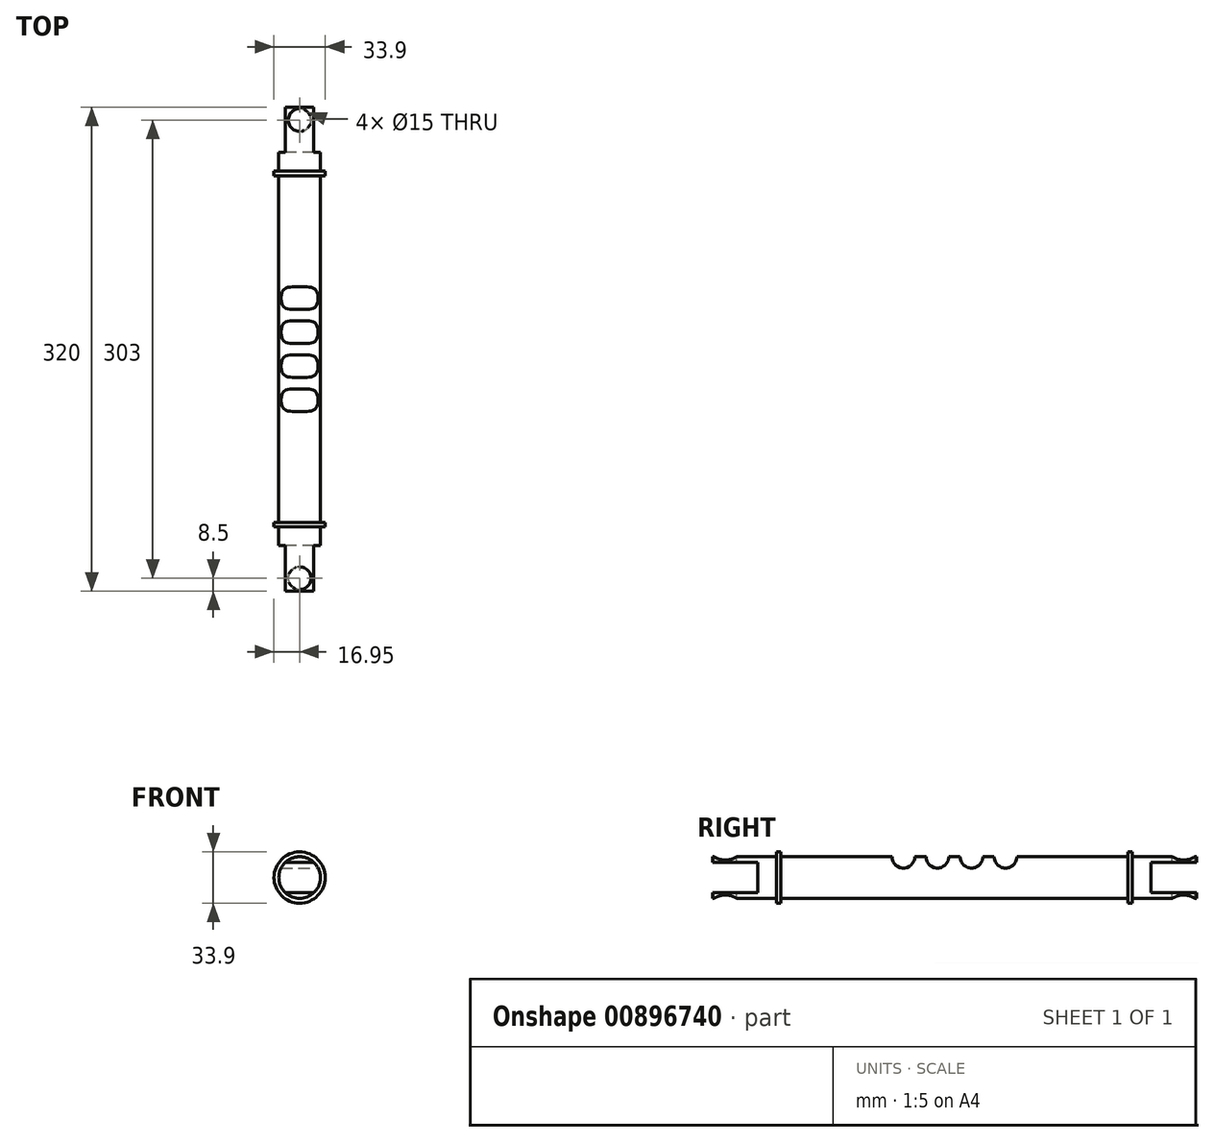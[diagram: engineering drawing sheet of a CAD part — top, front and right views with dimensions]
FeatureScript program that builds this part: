
annotation { "Feature Type Name" : "Feature", "Feature Type Description" : "" }
export const myFeature = defineFeature(function(context is Context, id is Id, definition is map)
    precondition{}
    {
        {
            var Q0;
            Q0=qCreatedBy(makeId("Front.planeOp"),FACE);
            var sketch = newSketch(context, id + "F0", { "sketchPlane" : qUnion([Q0])});
            skCircle(sketch, "E0", {"center": v(0, 0) * mm, "radius": 13.75 * mm});
            skSolve(sketch);
        }
        {
            var Q0;
            Q0=makeQuery(id+"F0.imprint","IMPRINT",FACE,{"disambiguationData":[TD([[makeQuery(id+"F0.imprint","IMPRINT",EDGE,{"derivedFrom":sQuery(id+"F0.wireOp",EDGE,"E0")}),1.0]])]});
            extrude(context, id + "F1", {"entities" : qUnion([Q0]), "depth" : 160 * mm, "offsetDistance" : 25 * mm});
        }
        {
            var Q0;
            Q0=qCreatedBy(makeId("Right.planeOp"),FACE);
            var sketch = newSketch(context, id + "F2", { "sketchPlane" : qUnion([Q0])});
            skLineSegment(sketch, "E1", {"start": v(-118.75, 13.75) * mm, "end": v(-133.75, 13.75) * mm});
            skArc(sketch, "E2", {"start": v(-156.25, 13.75) * mm, "mid": v(-148.75, 6.25) * mm, "end": v(-141.25, 13.75) * mm});
            skArc(sketch, "E3", {"start": v(-133.75, 13.75) * mm, "mid": v(-126.25, 6.25) * mm, "end": v(-118.75, 13.75) * mm});
            skPoint(sketch, "E4.orphan", {"position": v(-320, 13.75) * mm});
            skPoint(sketch, "E5.start.orphan", {"position": v(-160, 13.75) * mm});
            skPoint(sketch, "E6.orphan", {"position": v(0, 13.75) * mm});
            skPoint(sketch, "E7.orphan", {"position": v(0, -32.69) * mm});
            skLineSegment(sketch, "E8.trimOffspring", {"start": v(-141.25, 13.75) * mm, "end": v(-156.25, 13.75) * mm});
            skLineSegment(sketch, "E9", {"start": v(-160, 13.75) * mm, "end": v(-160, -55.7) * mm, "construction": true});
            skLineSegment(sketch, "E10", {"start": v(-9.6, 13.75) * mm, "end": v(-70.32, 13.75) * mm});
            skLineSegment(sketch, "E11.bottom", {"start": v(-42.38, 13.75) * mm, "end": v(-45.28, 13.75) * mm, "construction": true});
            skLineSegment(sketch, "E11.top", {"start": v(-42.38, 16.95) * mm, "end": v(-45.28, 16.95) * mm});
            skLineSegment(sketch, "E11.left", {"start": v(-42.38, 13.75) * mm, "end": v(-42.38, 16.95) * mm});
            skLineSegment(sketch, "E11.right", {"start": v(-45.28, 13.75) * mm, "end": v(-45.28, 16.95) * mm});
            skLineSegment(sketch, "E12", {"start": v(-1.56, 0) * mm, "end": v(-69.06, 0) * mm, "construction": true});
            skSolve(sketch);
        }
        {
            var Q0;
            Q0=makeQuery(id+"F2.imprint","IMPRINT",FACE,{"disambiguationData":[TD([[makeQuery(id+"F2.imprint","IMPRINT",EDGE,{"derivedFrom":sQuery(id+"F2.wireOp",EDGE,"nActoI5t-i0K3-M4oz-HlWf-qxMpZ23eEYZS")}),1.0]])]});
            var Q1;
            Q1=makeQuery(id+"F2.imprint","IMPRINT",FACE,{"disambiguationData":[TD([[makeQuery(id+"F2.imprint","IMPRINT",EDGE,{"derivedFrom":sQuery(id+"F2.wireOp",EDGE,"TeYV5sM8-H92p-1zPf-3jmj-FJZRoNFdDDTj")}),1.0]])]});
            var Q2;
            Q2=makeQuery(id+"F2.imprint","IMPRINT",FACE,{"disambiguationData":[TD([[makeQuery(id+"F2.imprint","IMPRINT",EDGE,{"derivedFrom":sQuery(id+"F2.wireOp",EDGE,"E2")}),1.0]])]});
            var Q3;
            Q3=makeQuery(id+"F2.imprint","IMPRINT",FACE,{"disambiguationData":[TD([[makeQuery(id+"F2.imprint","IMPRINT",EDGE,{"derivedFrom":sQuery(id+"F2.wireOp",EDGE,"E1")}),1.0]])]});
            extrude(context, id + "F3", {"entities" : qUnion([Q0, Q1, Q2, Q3]), "operationType" : NewBodyOperationType.REMOVE, "endBound" : BoundingType.SYMMETRIC, "oppositeDirection" : true, "depth" : 25 * mm, "offsetDistance" : 25 * mm});
        }
        {
            var Q0;
            Q0=qCreatedBy(makeId("Front.planeOp"),FACE);
            var sketch = newSketch(context, id + "F4", { "sketchPlane" : qUnion([Q0])});
            skLineSegment(sketch, "E13.bottom", {"start": v(18.75, 10) * mm, "end": v(-18.75, 10) * mm});
            skLineSegment(sketch, "E13.top", {"start": v(18.75, -10) * mm, "end": v(-18.75, -10) * mm});
            skLineSegment(sketch, "E13.left", {"start": v(18.75, 10) * mm, "end": v(18.75, -10) * mm});
            skLineSegment(sketch, "E13.right", {"start": v(-18.75, 10) * mm, "end": v(-18.75, -10) * mm});
            skPoint(sketch, "E13.middle", {"position": v(0, 0) * mm});
            skSolve(sketch);
        }
        {
            var Q0;
            Q0=makeQuery(id+"F4.imprint","IMPRINT",FACE,{"disambiguationData":[TD([[makeQuery(id+"F4.imprint","IMPRINT",EDGE,{"derivedFrom":sQuery(id+"F4.wireOp",EDGE,"E13.bottom")}),1.0]])]});
            extrude(context, id + "F5", {"entities" : qUnion([Q0]), "operationType" : NewBodyOperationType.REMOVE, "depth" : 30 * mm, "offsetDistance" : 25 * mm});
        }
        {
            var Q0;
            Q0=qCreatedBy(makeId("Top.planeOp"),FACE);
            var sketch = newSketch(context, id + "F6", { "sketchPlane" : qUnion([Q0])});
            skCircle(sketch, "E14", {"center": v(0, -8.5) * mm, "radius": 7.5 * mm});
            skSolve(sketch);
        }
        {
            var Q0;
            Q0=makeQuery(id+"F6.imprint","IMPRINT",FACE,{"disambiguationData":[TD([[makeQuery(id+"F6.imprint","IMPRINT",EDGE,{"derivedFrom":sQuery(id+"F6.wireOp",EDGE,"E14")}),1.0]])]});
            extrude(context, id + "F7", {"entities" : qUnion([Q0]), "operationType" : NewBodyOperationType.REMOVE, "endBound" : BoundingType.SYMMETRIC, "oppositeDirection" : true, "depth" : 2000 * mm, "offsetDistance" : 25 * mm});
        }
        {
            var Q0;
            Q0=makeQuery(id+"F2.imprint","IMPRINT",FACE,{"disambiguationData":[TD([[makeQuery(id+"F2.imprint","IMPRINT",EDGE,{"derivedFrom":sQuery(id+"F2.wireOp",EDGE,"E11.top")}),1.0]])]});
            var Q1;
            Q1=sQuery(id+"F2.wireOp",EDGE,"E12");
            revolve(context, id + "F8", {"operationType" : NewBodyOperationType.ADD, "surfaceOperationType" : NewSurfaceOperationType.NEW, "entities" : qUnion([Q0]), "axis" : qUnion([Q1]), "revolveType" : RevolveType.FULL});
        }
        {
            var Q0;
            Q0=makeQuery(id+"F1.opExtrude","SWEPT_BODY",BODY,{"disambiguationData":[OSD([sQuery(id+"F0.wireOp",EDGE,"E0")])]});
            var Q1;
            Q1=makeQuery(id+"F1.opExtrude","CAP_FACE",FACE,{"disambiguationData":[OSD([sQuery(id+"F0.wireOp",EDGE,"E0")])],"isStart":false});
            mirror(context, id + "F9", {"operationType" : NewBodyOperationType.ADD, "entities" : qUnion([Q0]), "mirrorPlane" : qUnion([Q1])});
        }
    });
